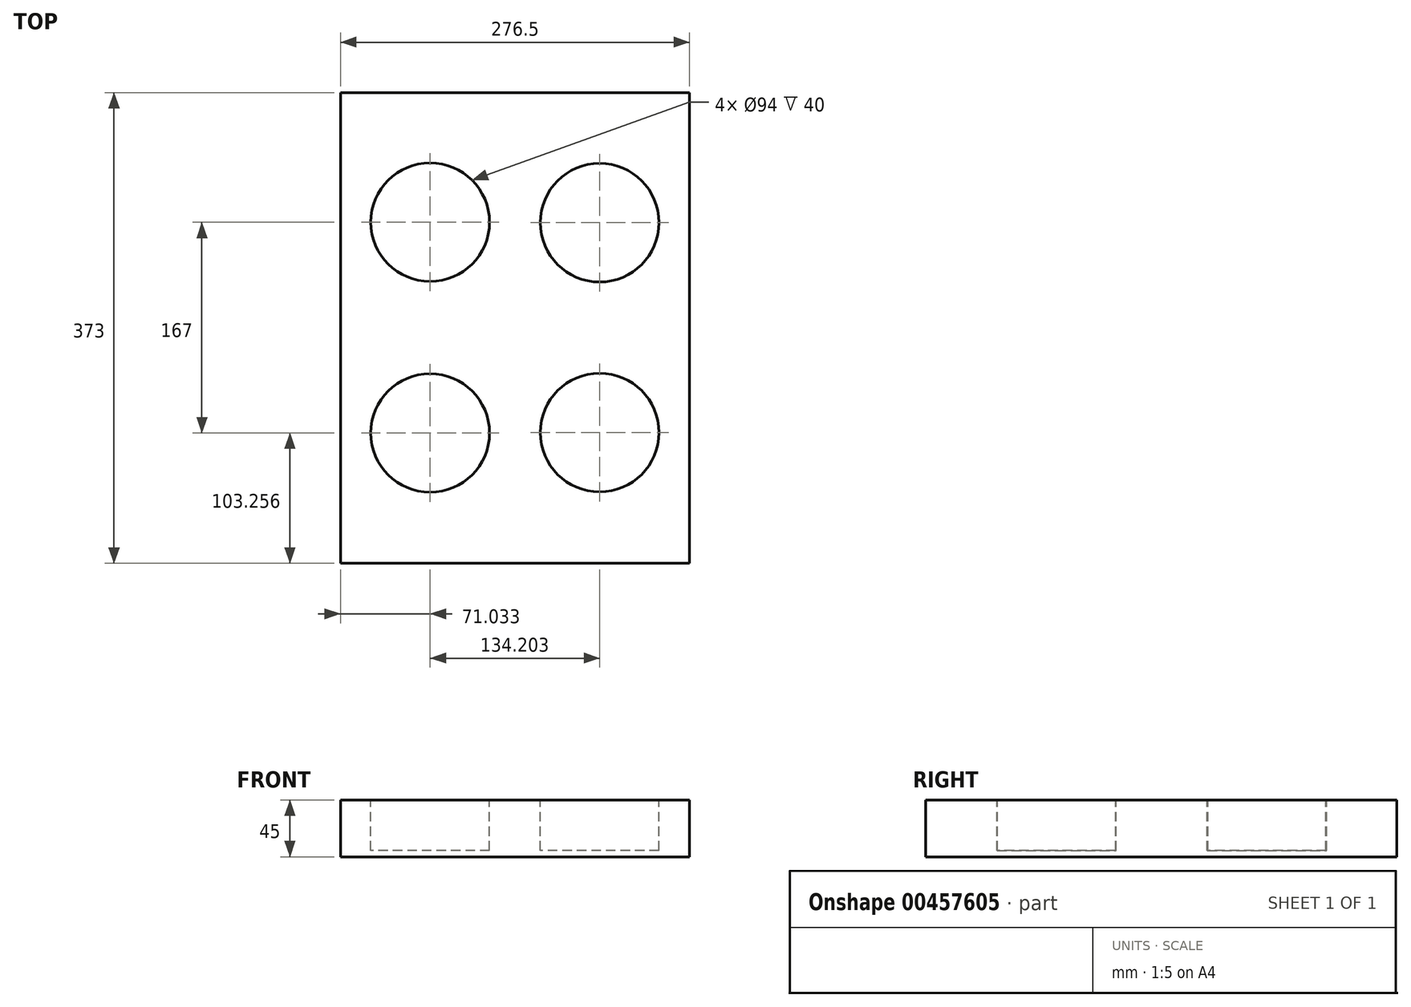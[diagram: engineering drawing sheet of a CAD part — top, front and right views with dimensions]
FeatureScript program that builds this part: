
annotation { "Feature Type Name" : "Feature", "Feature Type Description" : "" }
export const myFeature = defineFeature(function(context is Context, id is Id, definition is map)
    precondition{}
    {
        {
            var Q0;
            Q0=qCreatedBy(makeId("Top.planeOp"),FACE);
            var sketch = newSketch(context, id + "F0", { "sketchPlane" : qUnion([Q0])});
            skLineSegment(sketch, "E0.bottom", {"start": v(138.25, 186.5) * mm, "end": v(-138.25, 186.5) * mm});
            skLineSegment(sketch, "E0.top", {"start": v(138.25, -186.5) * mm, "end": v(-138.25, -186.5) * mm});
            skLineSegment(sketch, "E0.left", {"start": v(138.25, 186.5) * mm, "end": v(138.25, -186.5) * mm});
            skLineSegment(sketch, "E0.right", {"start": v(-138.25, 186.5) * mm, "end": v(-138.25, -186.5) * mm});
            skPoint(sketch, "E0.middle", {"position": v(0, 0) * mm});
            skSolve(sketch);
        }
        {
            var Q0;
            Q0=makeQuery(id+"F0.imprint","IMPRINT",FACE,{"disambiguationData":[TD([[makeQuery(id+"F0.imprint","IMPRINT",EDGE,{"derivedFrom":sQuery(id+"F0.wireOp",EDGE,"E0.bottom")}),1.0]])]});
            var sketch = newSketch(context, id + "F1", { "sketchPlane" : qUnion([Q0])});
            skLineSegment(sketch, "E1", {"start": v(-138.02, 186.76) * mm, "end": v(-67.22, 186.76) * mm, "construction": true});
            skLineSegment(sketch, "E2", {"start": v(-67.22, 186.76) * mm, "end": v(-67.22, 83.76) * mm, "construction": true});
            skCircle(sketch, "E3", {"center": v(-67.22, 83.76) * mm, "radius": 47 * mm});
            skLineSegment(sketch, "E4", {"start": v(137.79, 186.4) * mm, "end": v(66.99, 186.4) * mm, "construction": true});
            skLineSegment(sketch, "E5", {"start": v(66.99, 186.4) * mm, "end": v(66.99, 83.4) * mm, "construction": true});
            skCircle(sketch, "E6", {"center": v(66.99, 83.4) * mm, "radius": 47 * mm});
            skLineSegment(sketch, "E7", {"start": v(-138.02, 186.76) * mm, "end": v(-138.02, 0.26) * mm, "construction": true});
            skLineSegment(sketch, "E8", {"start": v(-138.02, 0.26) * mm, "end": v(138.44, 0.26) * mm, "construction": true});
            skCircle(sketch, "E9.MirrorC", {"center": v(-67.22, -83.24) * mm, "radius": 47 * mm});
            skCircle(sketch, "E10.MirrorC", {"center": v(66.99, -82.88) * mm, "radius": 47 * mm});
            skSolve(sketch);
        }
        {
            var Q0;
            Q0=makeQuery(id+"F0.imprint","IMPRINT",FACE,{"disambiguationData":[TD([[makeQuery(id+"F0.imprint","IMPRINT",EDGE,{"derivedFrom":sQuery(id+"F0.wireOp",EDGE,"E0.bottom")}),1.0]])]});
            extrude(context, id + "F2", {"entities" : qUnion([Q0]), "oppositeDirection" : true, "depth" : 45 * mm});
        }
        {
            var Q0;
            Q0 = qSketchRegion(id + "F1", true);
            extrude(context, id + "F3", {"entities" : qUnion([Q0]), "operationType" : NewBodyOperationType.REMOVE, "oppositeDirection" : true, "depth" : 40 * mm, "offsetDistance" : 25 * mm});
        }
    });
